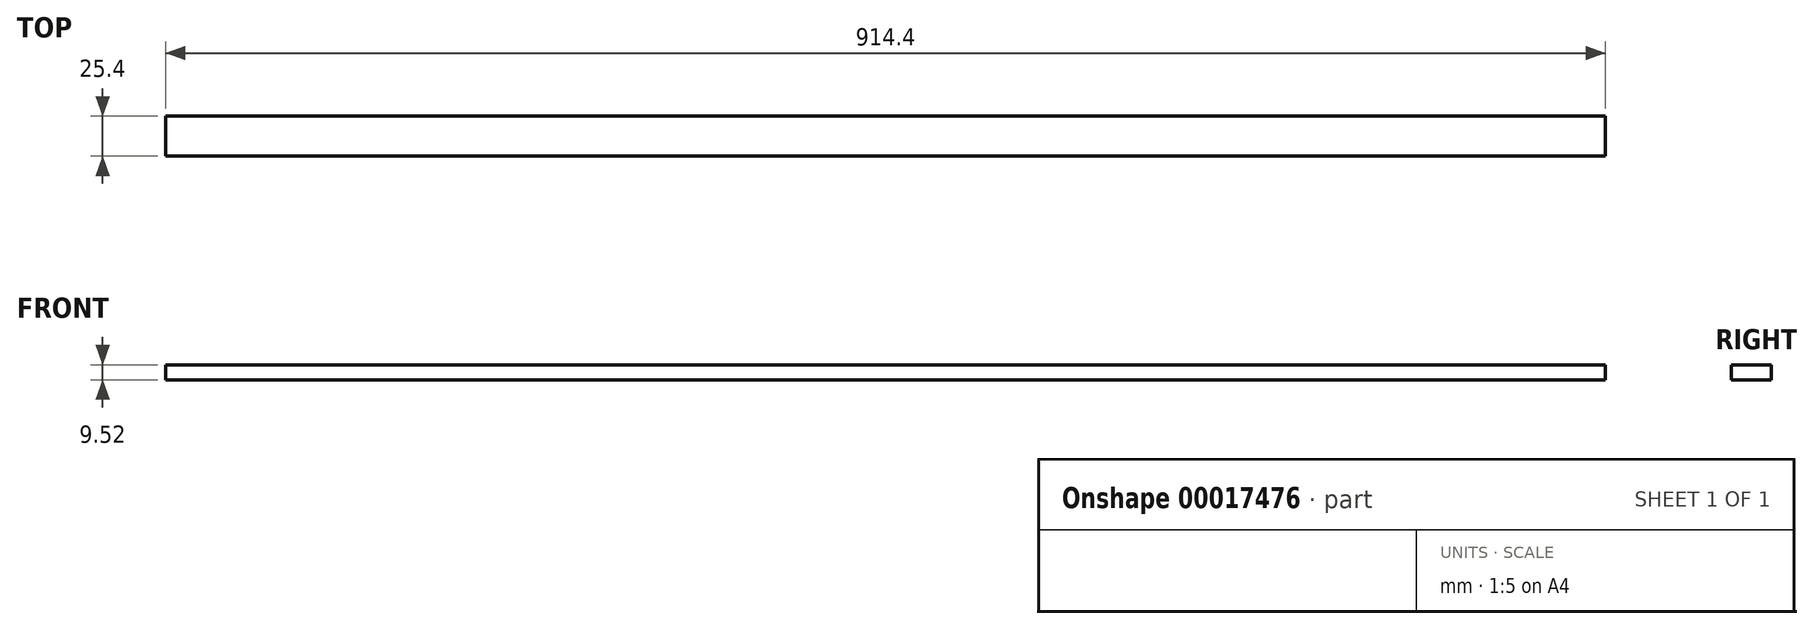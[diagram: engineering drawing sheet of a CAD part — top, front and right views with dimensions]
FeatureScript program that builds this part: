
annotation { "Feature Type Name" : "Feature", "Feature Type Description" : "" }
export const myFeature = defineFeature(function(context is Context, id is Id, definition is map)
    precondition{}
    {
        {
            var Q0;
            Q0=qCreatedBy(makeId("Front.planeOp"),FACE);
            var sketch = newSketch(context, id + "F0", { "sketchPlane" : qUnion([Q0])});
            skLineSegment(sketch, "E0.rect.bottom", {"start": v(-457.2, 4.76) * mm, "end": v(457.2, 4.76) * mm});
            skLineSegment(sketch, "E0.rect.top", {"start": v(-457.2, -4.76) * mm, "end": v(457.2, -4.76) * mm});
            skLineSegment(sketch, "E0.rect.left", {"start": v(-457.2, 4.76) * mm, "end": v(-457.2, -4.76) * mm});
            skLineSegment(sketch, "E0.rect.right", {"start": v(457.2, 4.76) * mm, "end": v(457.2, -4.76) * mm});
            skPoint(sketch, "E0.rect.middle", {"position": v(0, 0) * mm});
            skSolve(sketch);
        }
        {
            var Q0;
            Q0 = qSketchRegion(id + "F0", true);
            extrude(context, id + "F1", {"entities" : qUnion([Q0]), "depth" : 25.4 * mm});
        }
    });
